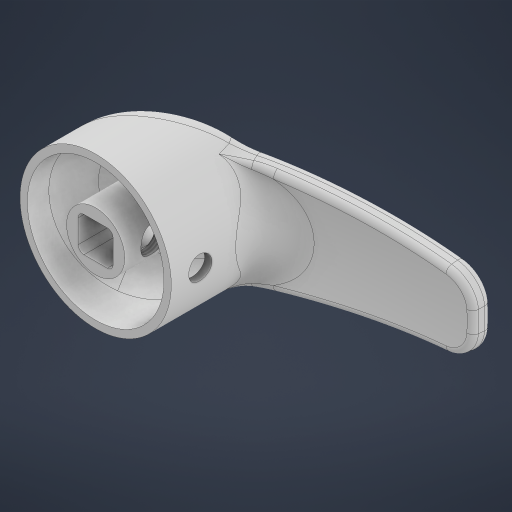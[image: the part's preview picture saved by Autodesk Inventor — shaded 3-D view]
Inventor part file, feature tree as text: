
AUTODESK INVENTOR PART (.ipt)
format: ipt  version: 2023 (Build 270158000, 158)  size: 905,728 bytes
history: native  units: mm
features: sketch x7, fillet x6, delete_face x4, extrude x3, other x3, plane x2, split x2, thicken_offset x2, boolean_combine x1, hole x1, sweep x1
ambient origin geometry x8: Origin, YZ Plane, XZ Plane, XY Plane, X Axis, Y Axis, Z Axis, Center Point
bodies: Solid1 (feature_tree), Solid2 (feature_tree)
feature tree (32):
  sketch  "Sketch1"  dims[d0=52.0mm d1=47.0mm d2=20.0mm d4=12.0mm d5=12.0mm d6=210.0mm d7=26.0mm]
  sketch  "Sketch2"  dims[d8=20.0mm d9=90.0mm]
  plane  "Work Plane1"
  sketch  "Sketch3"  dims[d10=46.0mm d11=101.2mm d12=100.0mm]
  sketch  "Sketch4"  dims[d13=52.0mm d14=25.0mm]
  split  "Split1"
  delete_face  "Delete Face1"
  thicken_offset  "Thicken1"
  extrude  "Extrusion1"  Depth=210.0mm
  delete_face  "Delete Face2"
  delete_face  "Delete Face3"
  fillet  "Fillet1"  Radius=20.0mm
  fillet  "Fillet2"  Radius=12.0mm
  fillet  "Fillet3"  Radius=12.0mm
  fillet  "Fillet4"  Radius=210.0mm
  fillet  "Fillet5"  Radius=26.0mm
  sketch  "Sketch5"  dims[d15=40.0mm d16=90.0mm]
  split  "Split2"
  delete_face  "Delete Face4"
  thicken_offset  "Thicken2"
  boolean_combine  "Combine1"
  plane  "Work Plane2"
  sketch  "Sketch6"  dims[d17=15.0mm]
  extrude  "Extrusion2"  Depth=90.0mm
  extrude  "Extrusion3"  Depth=101.2mm
  fillet  "Fillet6"  Radius=100.0mm
  hole  "Hole1"  [1 undecoded]
  other  "Srf1"
  other  "Srf2"
  sketch  "Sketch7"  dims[d18=10.0mm d19=0.0mm d20=0.0mm d21=6.0mm d22=6.0mm d23=10.0mm d24=0.0mm d25=2.0mm d26=2.0mm d27=2.0mm d28=3.5mm d29=12.0mm d30=8.5mm d31=15.0mm d32=2.0mm d33=2.0mm d34=15.0mm d35=5.94mm d36=3.0mm d37=5.0mm d38=3.0mm d39=5.0mm d40=2.0mm d41=2.0mm d42=2.0mm d43=2.0mm d44=15.0mm d45=5.0mm d46=2.0mm d47=24.0mm d48=52.0mm d49=2.5mm d50=0.5mm d51=0.5mm d52=1.0mm d53=1.0mm d54=45.0mm d55=8.0mm d56=10.0mm d57=4.5mm d58=10.0mm d59=0.0mm d60=10.0mm d61=0.0mm d62=2.0mm d63=8.917468mm d64=20.0mm d65=4.0mm d66=2.0mm d67=90.0deg d68=25.1mm d69=0.0mm d70=0.75mm d71=20.594885mm d72=0.0625mm d73=0.75mm d74=0.375mm]
  sweep  "SweepSrf1"
  other  "OffsetSrf1"
note: 1 required parameter value undecoded (feature->parameter linkage not recoverable at this tier; creation-order binding heuristic only, values carry confidence <= 0.55)
